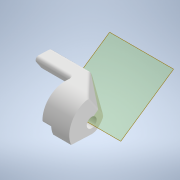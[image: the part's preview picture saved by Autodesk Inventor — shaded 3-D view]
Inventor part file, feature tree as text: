
AUTODESK INVENTOR PART (.ipt)
format: ipt  version: 2022 (Build 260153000, 153)  size: 295,424 bytes
history: native  units: mm
features: other x9, reference x6, extrude x5, sketch x5, projected_geometry x5, fillet x4, mirror x1
ambient origin geometry x8: Origin, YZ Plane, XZ Plane, XY Plane, X Axis, Y Axis, Z Axis, Center Point
bodies: Body1 (feature_tree)
feature tree (35):
  other  "Твердое тело1"
  extrude  "Выдавливание1"  Depth=3.4mm
  other  "РабПлоскость1"
  extrude  "Выдавливание2"  Depth=0.5mm
  fillet  "Сопряжение1"  Radius=3.0mm
  extrude  "Выдавливание3"  Depth=6.2mm TaperAngle=0.0deg
  fillet  "Сопряжение3"  Radius=2.0mm
  fillet  "Сопряжение4"  Radius=10.0mm
  other  "РабПлоскость2"
  extrude  "Выдавливание4"  Depth=1.0mm
  fillet  "Сопряжение5"  Radius=1.445133mm
  mirror  "Зеркальное отражение1"
  extrude  "Выдавливание5"  Depth=1.0mm
  sketch  "Эскиз1"
  reference  "Ссылка1"
  reference  "Ссылка2"
  sketch  "Эскиз2"
  projected_geometry  "Спроецированная петля1"
  reference  "Ссылка3"
  reference  "Ссылка4"
  sketch  "Эскиз3"
  reference  "Ссылка5"
  projected_geometry  "Спроецированная петля2"
  projected_geometry  "Спроецированная петля3"
  other  "РабОсь1"
  sketch  "Эскиз4"
  reference  "Ссылка6"
  projected_geometry  "Спроецированная петля4"
  projected_geometry  "Спроецированная петля5"
  sketch  "Эскиз5"
  other  "<userpath>\Documents\Git\MZCAT_2024\MZCAT_3.iam"
  other  "MZCAT_3.iam"
  other  "base:1"
  other  "base plate:2"
  other  "Linit Switch:2"
